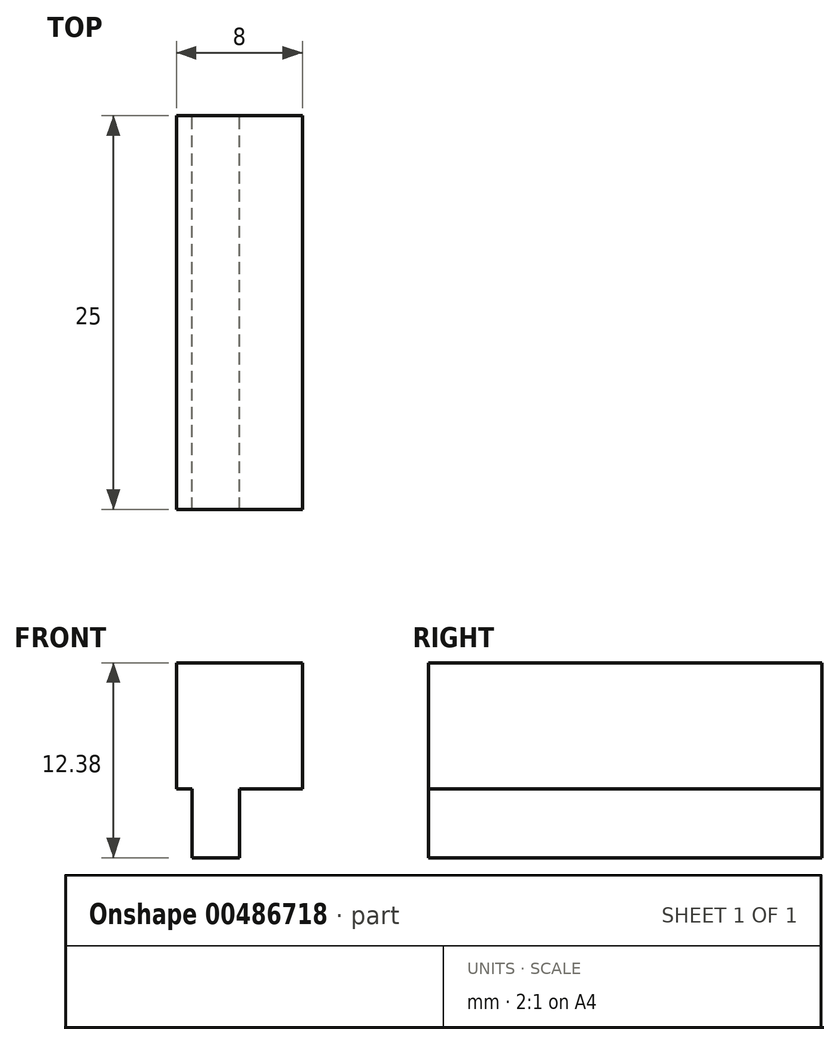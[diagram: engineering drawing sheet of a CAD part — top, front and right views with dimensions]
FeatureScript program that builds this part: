
annotation { "Feature Type Name" : "Feature", "Feature Type Description" : "" }
export const myFeature = defineFeature(function(context is Context, id is Id, definition is map)
    precondition{}
    {
        {
            var Q0;
            Q0=qCreatedBy(makeId("Front.planeOp"),FACE);
            var sketch = newSketch(context, id + "F0", { "sketchPlane" : qUnion([Q0])});
            skLineSegment(sketch, "E0.bottom", {"start": v(0, 0) * mm, "end": v(4, 0) * mm});
            skLineSegment(sketch, "E0.top", {"start": v(0, 8) * mm, "end": v(4, 8) * mm});
            skLineSegment(sketch, "E0.left", {"start": v(0, 0) * mm, "end": v(0, 8) * mm});
            skLineSegment(sketch, "E0.right", {"start": v(4, 0) * mm, "end": v(4, 8) * mm});
            skLineSegment(sketch, "E1.bottom", {"start": v(0, 0) * mm, "end": v(3, 0) * mm});
            skLineSegment(sketch, "E1.top", {"start": v(0, -4.38) * mm, "end": v(3, -4.38) * mm});
            skLineSegment(sketch, "E1.left", {"start": v(0, 0) * mm, "end": v(0, -4.38) * mm});
            skLineSegment(sketch, "E1.right", {"start": v(3, 0) * mm, "end": v(3, -4.38) * mm});
            skLineSegment(sketch, "E2.MirrorCS", {"start": v(0, 8) * mm, "end": v(-4, 8) * mm});
            skLineSegment(sketch, "E3.MirrorCS", {"start": v(-4, 0) * mm, "end": v(-4, 8) * mm});
            skLineSegment(sketch, "E4.MirrorCS", {"start": v(0, 0) * mm, "end": v(-4, 0) * mm});
            skLineSegment(sketch, "E5.MirrorCS", {"start": v(-3, 0) * mm, "end": v(-3, -4.38) * mm});
            skLineSegment(sketch, "E6.MirrorCS", {"start": v(0, -4.38) * mm, "end": v(-3, -4.38) * mm});
            skSolve(sketch);
        }
        {
            var Q0;
            {var subQ1=sQuery(id+"F0.wireOp",EDGE,"E0.left");Q0=makeQuery(id+"F0.imprint","IMPRINT",FACE,{"disambiguationData":[TD([[makeQuery(id+"F0.imprint","IMPRINT",EDGE,{"derivedFrom":subQ1}),1.0]])]});}
            var Q1;
            Q1=makeQuery(id+"F0.imprint","IMPRINT",FACE,{"disambiguationData":[TD([[makeQuery(id+"F0.imprint","IMPRINT",EDGE,{"derivedFrom":sQuery(id+"F0.wireOp",EDGE,"E0.bottom")}),1.0]])]});
            var Q2;
            {var subQ0=sQuery(id+"F0.wireOp",EDGE,"E1.left");Q2=makeQuery(id+"F0.imprint","IMPRINT",FACE,{"disambiguationData":[TD([[makeQuery(id+"F0.imprint","IMPRINT",EDGE,{"derivedFrom":subQ0}),-1.0]])]});}
            var Q3;
            Q3=makeQuery(id+"F0.imprint","IMPRINT",FACE,{"disambiguationData":[TD([[makeQuery(id+"F0.imprint","IMPRINT",EDGE,{"derivedFrom":sQuery(id+"F0.wireOp",EDGE,"E1.bottom")}),-1.0]])]});
            extrude(context, id + "F1", {"entities" : qUnion([Q0, Q1, Q2, Q3]), "depth" : 25 * mm});
        }
    });
